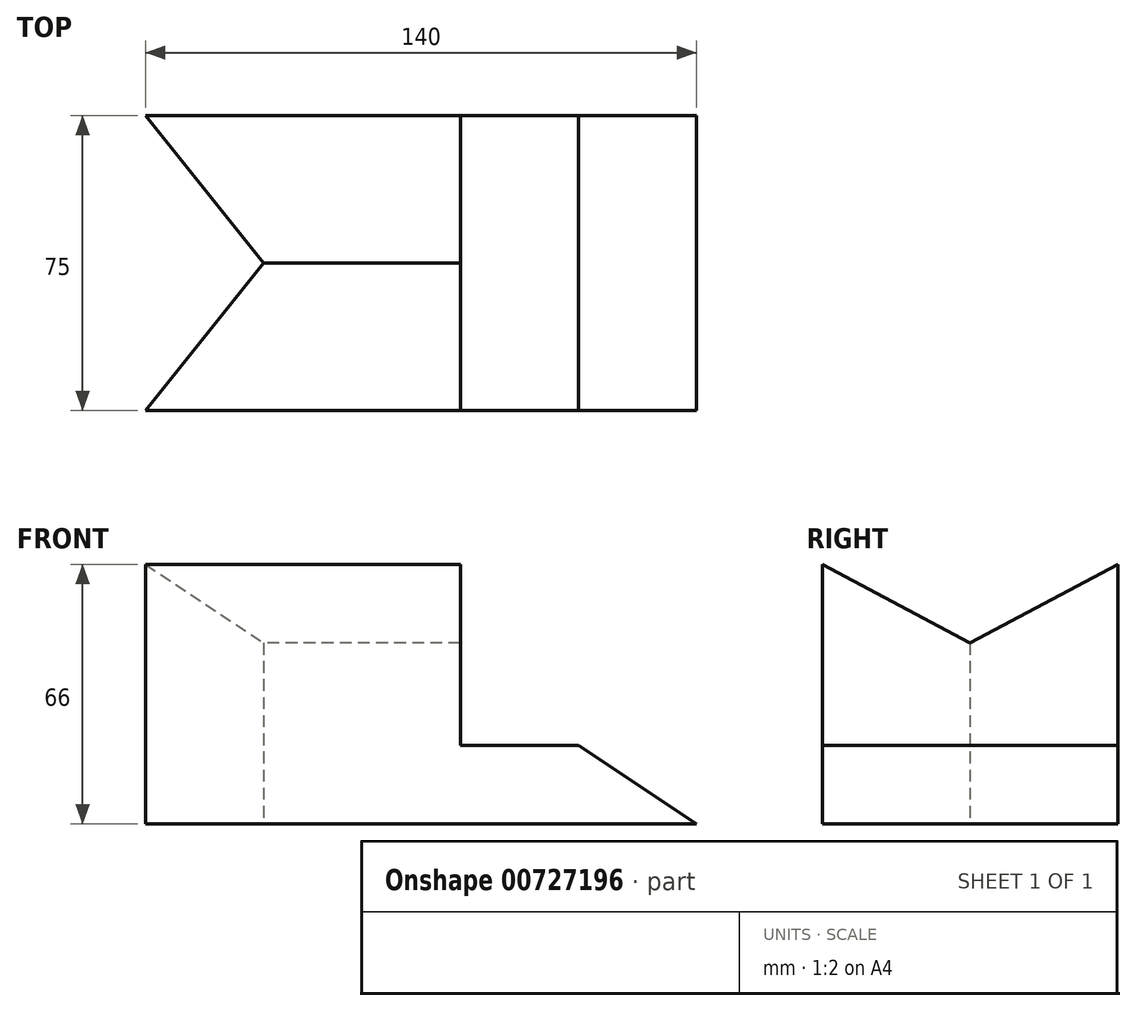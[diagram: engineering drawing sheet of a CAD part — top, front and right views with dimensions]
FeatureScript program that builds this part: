
annotation { "Feature Type Name" : "Feature", "Feature Type Description" : "" }
export const myFeature = defineFeature(function(context is Context, id is Id, definition is map)
    precondition{}
    {
        {
            var Q0;
            Q0=qCreatedBy(makeId("Right.planeOp"),FACE);
            var sketch = newSketch(context, id + "F0", { "sketchPlane" : qUnion([Q0])});
            skLineSegment(sketch, "E0.bottom", {"start": v(37.5, -33) * mm, "end": v(-37.5, -33) * mm});
            skLineSegment(sketch, "E0.top", {"start": v(37.5, 33) * mm, "end": v(-37.5, 33) * mm, "construction": true});
            skLineSegment(sketch, "E0.left", {"start": v(37.5, -33) * mm, "end": v(37.5, 33) * mm});
            skLineSegment(sketch, "E0.right", {"start": v(-37.5, -33) * mm, "end": v(-37.5, 33) * mm});
            skPoint(sketch, "E0.middle", {"position": v(0, 0) * mm});
            skLineSegment(sketch, "E1", {"start": v(0, 33) * mm, "end": v(0, 13) * mm, "construction": true});
            skLineSegment(sketch, "E2", {"start": v(0, 13) * mm, "end": v(-37.5, 33) * mm});
            skLineSegment(sketch, "E3.MirrorCS", {"start": v(0, 13) * mm, "end": v(37.5, 33) * mm});
            skSolve(sketch);
        }
        {
            var Q0;
            {var subQ2=sQuery(id+"F0.wireOp",EDGE,"E0.bottom");Q0=makeQuery(id+"F0.imprint","IMPRINT",FACE,{"disambiguationData":[TD([[makeQuery(id+"F0.imprint","IMPRINT",EDGE,{"derivedFrom":subQ2}),-1.0]])]});}
            extrude(context, id + "F1", {"entities" : qUnion([Q0]), "depth" : 140 * mm, "offsetDistance" : 25 * mm, "symmetric" : true});
        }
        {
            var Q0;
            Q0=makeQuery(id+"F1.opExtrude","SWEPT_FACE",FACE,{"disambiguationData":[OSD([sQuery(id+"F0.wireOp",EDGE,"E0.right")])]});
            var sketch = newSketch(context, id + "F2", { "sketchPlane" : qUnion([Q0])});
            skLineSegment(sketch, "E4.0", {"start": v(40, -13) * mm, "end": v(10, -13) * mm});
            skLineSegment(sketch, "E5.0", {"start": v(10, -13) * mm, "end": v(10, 33) * mm});
            skLineSegment(sketch, "E6", {"start": v(40, -13) * mm, "end": v(70, -33) * mm});
            skSolve(sketch);
        }
        {
            var Q0;
            Q0=makeQuery(id+"F2.imprint","IMPRINT",FACE,{"disambiguationData":[TD([[makeQuery(id+"F2.imprint","IMPRINT",EDGE,{"derivedFrom":sQuery(id+"F2.wireOp",EDGE,"E4.0")}),-1.0]])]});
            extrude(context, id + "F3", {"entities" : qUnion([Q0]), "operationType" : NewBodyOperationType.REMOVE, "endBound" : BoundingType.THROUGH_ALL, "oppositeDirection" : true, "depth" : 25 * mm, "offsetDistance" : 25 * mm});
        }
        {
            var Q0;
            Q0=makeQuery(id+"F1.opExtrude","SWEPT_FACE",FACE,{"disambiguationData":[OSD([sQuery(id+"F0.wireOp",EDGE,"E0.bottom")])]});
            var sketch = newSketch(context, id + "F4", { "sketchPlane" : qUnion([Q0])});
            skLineSegment(sketch, "E7", {"start": v(-70, 0) * mm, "end": v(-40, 0) * mm, "construction": true});
            skLineSegment(sketch, "E8", {"start": v(-40, 0) * mm, "end": v(-70, -37.5) * mm});
            skLineSegment(sketch, "E9", {"start": v(-40, 0) * mm, "end": v(-70, 37.5) * mm});
            skSolve(sketch);
        }
        {
            var Q0;
            Q0=makeQuery(id+"F4.imprint","IMPRINT",FACE,{"disambiguationData":[TD([[makeQuery(id+"F4.imprint","IMPRINT",EDGE,{"derivedFrom":sQuery(id+"F4.wireOp",EDGE,"E8")}),-1.0]])]});
            extrude(context, id + "F5", {"entities" : qUnion([Q0]), "operationType" : NewBodyOperationType.REMOVE, "endBound" : BoundingType.THROUGH_ALL, "oppositeDirection" : true, "depth" : 25 * mm, "offsetDistance" : 25 * mm});
        }
    });
